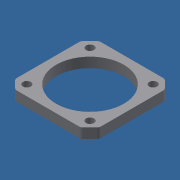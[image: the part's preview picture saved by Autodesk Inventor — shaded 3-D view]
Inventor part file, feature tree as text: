
AUTODESK INVENTOR PART (.ipt)
format: ipt  version: 2018 (Build 220112000, 112)  size: 200,192 bytes
history: native  units: mm
features: extrude x6, sketch x6, other x3, reference x1, projected_geometry x1
ambient origin geometry x8: Origin, YZ Plane, XZ Plane, XY Plane, X Axis, Y Axis, Z Axis, Center Point
bodies: Solid1 (feature_tree)
feature tree (17):
  extrude  "Extrusion1"  Depth=4.0mm
  extrude  "Extrusion3"  Depth=4.0mm
  extrude  "Extrusion4"  Depth=5.0mm TaperAngle=0.0deg
  extrude  "Extrusion5"  Depth=5.0mm
  extrude  "Extrusion6"  Depth=20.0mm
  extrude  "Extrusion7"  Depth=5.0mm TaperAngle=0.0deg
  sketch  "Sketch1"  dims[d0=24.0mm d1=4.0mm]
  reference  "Reference1"
  sketch  "Sketch3"  dims[d2=4.0mm d3=4.0mm]
  sketch  "Sketch4"  dims[d4=4.0mm d5=5.0mm d6=0.0mm]
  projected_geometry  "Projected Loop1"
  sketch  "Sketch5"  dims[d11=5.0mm d12=5.0mm]
  sketch  "Sketch6"  dims[d13=20.0mm d14=20.0mm]
  sketch  "Sketch7"  dims[d15=40.0mm d16=0.0mm d17=5.0mm d18=0.0mm d19=5.0mm d20=5.0mm d21=10.0mm d22=10.0mm d23=20.0mm d24=10.0mm d25=5.0mm d26=0.0mm d27=10.0mm d28=10.0mm d29=5.0mm d30=5.0mm d31=20.0mm d32=10.0mm d33=5.0mm d34=0.0mm d35=0.5mm d36=0.5mm d37=35.0mm d38=0.0mm]
  other  "<userpath>\OneDrive\Objet3D\3DPrinter\3DPrinterBeltCoreXY.iam"
  other  "3DPrinterBeltCoreXY.iam"
  other  "E3D Stepper Motor:1"
